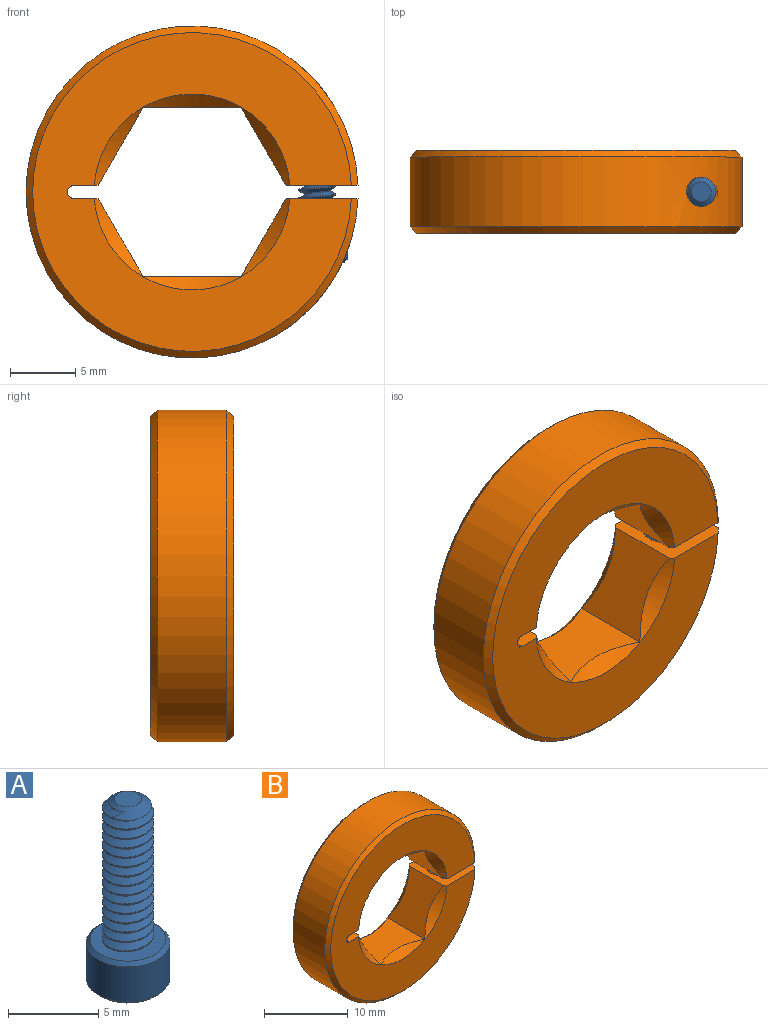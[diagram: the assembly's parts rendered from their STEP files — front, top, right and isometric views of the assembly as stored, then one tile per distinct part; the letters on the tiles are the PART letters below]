
ASSEMBLY  parts=2 mates=1
PART A: 24 faces, bbox 5.2x5.2x13 mm
  f0: cone r=2.32mm half-angle=45deg, axis (0,0,-1), area 4.6mm2, adj f1,f8
  f1: plane 4.43x4.43mm, normal (0,0,1), area 9mm2, adj f0,f2,f5,f6,f7
  f2: bspline ~9.82x2.84mm, area 52.8mm2, adj f1,f3,f5,f7
  f3: cone r=0.76mm half-angle=55deg, axis (0,0,-1), area 3.6mm2, adj f2,f4,f5,f6,f7
  f4: plane 1.51x1.51mm, normal (0,0,1), area 1.8mm2, adj f3
  f5: cylinder r=1.01mm len=9.35mm, axis (0,0,-1), area 7.4mm2, adj f1,f2,f3,f6
  f6: bspline ~9.59x2.84mm, area 52.8mm2, adj f1,f3,f5,f7
  f7: cylinder r=1.42mm len=9.06mm, axis (0,0,1), area 10.1mm2, adj f1,f2,f3,f6
  f8: cylinder r=2.32mm len=4.65mm, axis (0,0,1), area 34.8mm2, adj f0,f9
  f9: cone r=2.09mm half-angle=45deg, axis (0,0,1), area 4.6mm2, adj f8,f10
  f10: plane 4.63x4.63mm, normal (0,0,-1), area 7.8mm2, adj f9,f11,f19,f20,f21,f22,f23
  f11: cone r=1.37mm half-angle=45deg, axis (0,0,-1), area 0mm2, adj f10,f12
  f12: plane 2.31x1.71mm, normal (-0.5,-0.87,0), area 2.3mm2, adj f11,f13,f17,f18
  f13: plane 2.75x2.38mm, normal (0,0,-1), area 4.9mm2, adj f12,f14,f15,f16,f17,f18
  f14: plane 1.92x1.51mm, normal (1,0,0), area 2.3mm2, adj f13,f15,f18,f22
  f15: plane 2.31x1.71mm, normal (0.5,0.87,0), area 2.3mm2, adj f13,f14,f16,f21
  f16: plane 2.31x1.71mm, normal (-0.5,0.87,0), area 2.3mm2, adj f13,f15,f17,f20
  f17: plane 2.31x1.9mm, normal (-1,0,0), area 2.3mm2, adj f12,f13,f16,f19
  f18: plane 2.31x1.71mm, normal (0.5,-0.87,0), area 2.3mm2, adj f12,f13,f14,f23
  f19: cone r=1.37mm half-angle=45deg, axis (0,0,-1), area 0mm2, adj f10,f17
  f20: cone r=1.37mm half-angle=45deg, axis (0,0,-1), area 0mm2, adj f10,f16
  f21: cone r=1.37mm half-angle=45deg, axis (0,0,-1), area 0mm2, adj f10,f15
  f22: cone r=1.37mm half-angle=45deg, axis (0,0,-1), area 0.2mm2, adj f10,f14
  f23: cone r=1.37mm half-angle=45deg, axis (0,0,-1), area 0mm2, adj f10,f18
PART B: 24 faces, bbox 25.4x6.4x25.4 mm
  f0: cone r=12.19mm half-angle=45deg, axis (0,1,0), area 55.5mm2, adj f4,f5,f7,f8
  f1: cylinder r=2.38mm len=7.94mm, axis (0,0,1), area 80.2mm2, adj f4,f9
  f2: cylinder r=1.63mm len=3.26mm, axis (0,0,1), area 20.8mm2, adj f8,f9
  f3: cylinder r=1.13mm len=8.99mm, axis (0,0,-1), area 55.1mm2, adj f4,f7
  f4: cylinder r=12.7mm len=25.4mm, axis (0,1,0), area 385.2mm2, adj f0,f1,f3,f7,f8,f23
  f5: plane 24.38x24.37mm, normal (0,-1,0), area 284mm2, adj f0,f7,f8,f10,f11,f12,f13,f14
  f6: plane 24.38x24.37mm, normal (0,1,0), area 284mm2, adj f7,f8,f10,f11,f12,f15,f16,f23
  f7: plane 6.35x5.5mm, normal (0,0,-1), area 30.6mm2, adj f0,f3,f4,f5,f6,f13,f15,f22
  f8: plane 6.35x5.5mm, normal (0,0,1), area 26.2mm2, adj f0,f2,f4,f5,f6,f14,f16,f17
  f9: plane 4.76x4.76mm, normal (0,0,-1), area 9.4mm2, adj f1,f2
  f10: plane 6.35x1.84mm, normal (0,0,1), area 11.6mm2, adj f5,f6,f12,f14,f16,f18
  f11: plane 6.35x1.84mm, normal (0,0,-1), area 11.6mm2, adj f5,f6,f12,f13,f15,f20
  f12: cylinder r=0.5mm len=6.35mm, axis (0,-1,0), area 10mm2, adj f5,f6,f10,f11
  f13: cone r=6.48mm half-angle=45deg, axis (0,-1,0), area 21.7mm2, adj f5,f7,f11,f20,f21,f22
  f14: cone r=6.48mm half-angle=45deg, axis (0,-1,0), area 21.7mm2, adj f5,f8,f10,f17,f18,f19
  f15: cone r=7.49mm half-angle=45deg, axis (0,1,0), area 21.7mm2, adj f6,f7,f11,f20,f21,f22
  f16: cone r=7.49mm half-angle=45deg, axis (0,1,0), area 21.7mm2, adj f6,f8,f10,f17,f18,f19
  f17: plane 6.32x5.98mm, normal (-0.87,0,0.5), area 33.9mm2, adj f8,f14,f16,f19
  f18: plane 6.32x5.98mm, normal (0.87,0,0.5), area 34mm2, adj f10,f14,f16,f19
  f19: plane 7.48x6.32mm, normal (0,0,1), area 37.4mm2, adj f14,f16,f17,f18
  f20: plane 6.32x5.98mm, normal (0.87,0,-0.5), area 33.9mm2, adj f11,f13,f15,f21
  f21: plane 7.48x6.32mm, normal (0,0,-1), area 37.5mm2, adj f13,f15,f20,f22
  f22: plane 6.32x5.98mm, normal (-0.87,0,-0.5), area 33.9mm2, adj f7,f13,f15,f21
  f23: cone r=12.7mm half-angle=45deg, axis (0,-1,0), area 55.5mm2, adj f4,f6,f7,f8
PLACE A at identity
PLACE B at identity
MATE fastened A.f0 <-> B.f1  axis (0,0,1) through (9.57,0,-2.53)mm
